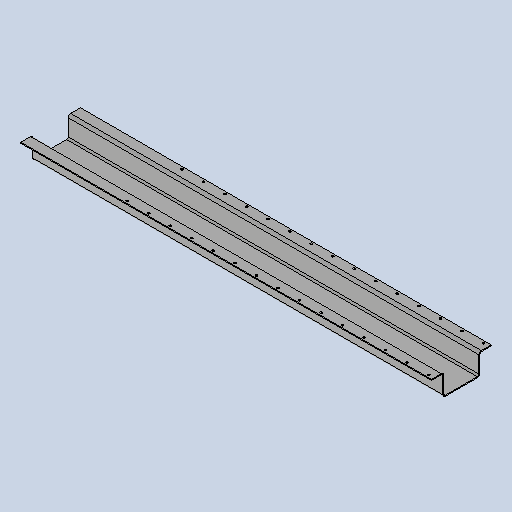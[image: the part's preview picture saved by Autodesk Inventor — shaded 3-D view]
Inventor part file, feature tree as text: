
AUTODESK INVENTOR PART (.ipt)
format: ipt  version: 2025 (Build 290162010, 162A)  size: 237,568 bytes
history: native  units: mm
features: sheet_metal_op x7, other x5, sketch x4, pattern_linear x1, mirror x1
ambient origin geometry x8: Origin, YZ Plane, XZ Plane, XY Plane, X Axis, Y Axis, Z Axis, Center Point
bodies: Solid1 (feature_tree)
feature tree (18):
  sheet_metal_op  "Face1"
  sheet_metal_op  "Flange4"
  sheet_metal_op  "Flange5"
  pattern_linear  "Rectangular Pattern2"  Count1=12  [1 undecoded]
  mirror  "Mirror2"
  sketch  "Sketch1"  dims[d5=1335.0mm]
  other  "Plate1"
  sketch  "Sketch6"  dims[d6=3.0mm d30=120.0mm]
  other  "Plate5"
  sheet_metal_op  "Bend4"
  sheet_metal_op  "Corner4"
  sketch  "Sketch9"  dims[d60=3.0mm]
  other  "Plate6"
  sheet_metal_op  "Bend5"
  sheet_metal_op  "Corner5"
  sketch  "Sketch11"  dims[d61=1.5mm d62=6.0mm d63=5.0mm d64=70.0mm d65=90.0deg d66=5.0mm d67=12.0mm d68=3.0mm d69=5.0mm d81=3.0mm d82=1.5mm d83=6.0mm d84=5.0mm d85=40.0mm d86=90.0deg d87=5.0mm d88=12.0mm d89=3.0mm d90=5.0mm d102=7.0mm d112=3.0mm d113=0.0mm d114=150.0mm d116=70.0mm d132=8.0mm d133=17.0mm]
  other  "Cut1"
  other  "Definition1"
note: 1 required parameter value undecoded (feature->parameter linkage not recoverable at this tier; creation-order binding heuristic only, values carry confidence <= 0.55)
